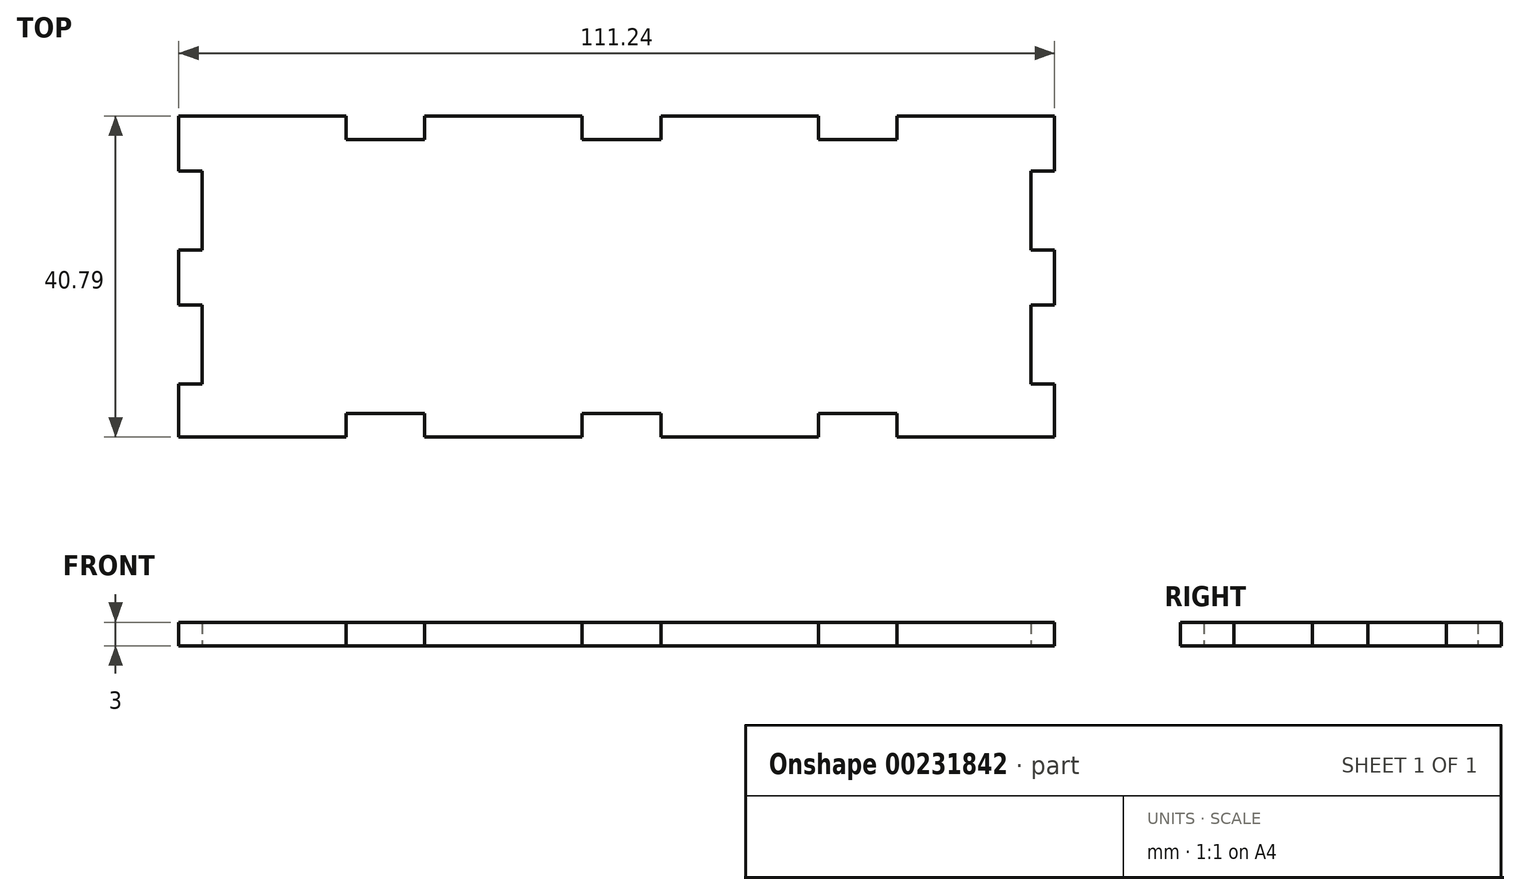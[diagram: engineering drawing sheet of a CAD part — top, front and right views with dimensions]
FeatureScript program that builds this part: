
annotation { "Feature Type Name" : "Feature", "Feature Type Description" : "" }
export const myFeature = defineFeature(function(context is Context, id is Id, definition is map)
    precondition{}
    {
        {
            var Q0;
            Q0=qCreatedBy(makeId("Top.planeOp"),FACE);
            var sketch = newSketch(context, id + "F0", { "sketchPlane" : qUnion([Q0])});
            skLineSegment(sketch, "E0", {"start": v(0, 0) * mm, "end": v(0, 7) * mm});
            skLineSegment(sketch, "E1", {"start": v(0, 7) * mm, "end": v(-3, 7) * mm});
            skLineSegment(sketch, "E2", {"start": v(-3, 7) * mm, "end": v(-3, 17) * mm});
            skLineSegment(sketch, "E3", {"start": v(0, 17) * mm, "end": v(-3, 17) * mm});
            skLineSegment(sketch, "E4", {"start": v(0, 17) * mm, "end": v(0, 24) * mm});
            skLineSegment(sketch, "E5", {"start": v(0, 24) * mm, "end": v(-3, 24) * mm});
            skLineSegment(sketch, "E6", {"start": v(-3, 24) * mm, "end": v(-3, 34) * mm});
            skLineSegment(sketch, "E7", {"start": v(-3, 34) * mm, "end": v(0, 34) * mm});
            skLineSegment(sketch, "E8", {"start": v(0, 34) * mm, "end": v(0, 41) * mm});
            skLineSegment(sketch, "E9", {"start": v(0, 41) * mm, "end": v(-20, 41) * mm});
            skLineSegment(sketch, "E10", {"start": v(-20, 41) * mm, "end": v(-20, 38) * mm});
            skLineSegment(sketch, "E11", {"start": v(-20, 38) * mm, "end": v(-30, 38) * mm});
            skLineSegment(sketch, "E12", {"start": v(-30, 41) * mm, "end": v(-30, 38) * mm});
            skLineSegment(sketch, "E13", {"start": v(-30, 41) * mm, "end": v(-50, 41) * mm});
            skLineSegment(sketch, "E14", {"start": v(-50, 38) * mm, "end": v(-50, 41) * mm});
            skLineSegment(sketch, "E15", {"start": v(-50, 38) * mm, "end": v(-60, 38) * mm});
            skLineSegment(sketch, "E16", {"start": v(-60, 38) * mm, "end": v(-60, 41) * mm});
            skLineSegment(sketch, "E17", {"start": v(-60, 41) * mm, "end": v(-80, 41) * mm});
            skLineSegment(sketch, "E18", {"start": v(-80, 38) * mm, "end": v(-80, 41) * mm});
            skLineSegment(sketch, "E19", {"start": v(-80, 38) * mm, "end": v(-90, 38) * mm});
            skLineSegment(sketch, "E20", {"start": v(-90, 41) * mm, "end": v(-90, 38) * mm});
            skLineSegment(sketch, "E21", {"start": v(-90, 41) * mm, "end": v(-110, 41) * mm});
            skLineSegment(sketch, "E22.MirrorCS", {"start": v(-50, 3.2) * mm, "end": v(-50, 0.2) * mm});
            skLineSegment(sketch, "E23.MirrorCS", {"start": v(-60, 3.2) * mm, "end": v(-60, 0.2) * mm});
            skLineSegment(sketch, "E24.MirrorCS", {"start": v(-80, 3.2) * mm, "end": v(-80, 0.2) * mm});
            skLineSegment(sketch, "E25.MirrorCS", {"start": v(-90, 0.2) * mm, "end": v(-90, 3.2) * mm});
            skLineSegment(sketch, "E26.MirrorCS", {"start": v(-20, 0.2) * mm, "end": v(-20, 3.2) * mm});
            skLineSegment(sketch, "E27.MirrorCS", {"start": v(-30, 0.2) * mm, "end": v(-30, 3.2) * mm});
            skLineSegment(sketch, "E28.MirrorCS", {"start": v(-90, 0.2) * mm, "end": v(-110, 0.2) * mm});
            skLineSegment(sketch, "E29.MirrorCS", {"start": v(-50, 3.2) * mm, "end": v(-60, 3.2) * mm});
            skLineSegment(sketch, "E30.MirrorCS", {"start": v(-30, 0.2) * mm, "end": v(-50, 0.2) * mm});
            skLineSegment(sketch, "E31.MirrorCS", {"start": v(-60, 0.2) * mm, "end": v(-80, 0.2) * mm});
            skLineSegment(sketch, "E32.MirrorCS", {"start": v(0, 0.2) * mm, "end": v(-20, 0.2) * mm});
            skLineSegment(sketch, "E33.MirrorCS", {"start": v(0, 7.2) * mm, "end": v(0, 0.2) * mm});
            skLineSegment(sketch, "E34.MirrorCS", {"start": v(-80, 3.2) * mm, "end": v(-90, 3.2) * mm});
            skLineSegment(sketch, "E35.MirrorCS", {"start": v(-20, 3.2) * mm, "end": v(-30, 3.2) * mm});
            skLineSegment(sketch, "E36.MirrorCS", {"start": v(-111.24, 7) * mm, "end": v(-108.24, 7) * mm});
            skLineSegment(sketch, "E37.MirrorCS", {"start": v(-108.24, 34) * mm, "end": v(-111.24, 34) * mm});
            skLineSegment(sketch, "E38.MirrorCS", {"start": v(-111.24, 17) * mm, "end": v(-108.24, 17) * mm});
            skLineSegment(sketch, "E39.MirrorCS", {"start": v(-111.24, 24) * mm, "end": v(-108.24, 24) * mm});
            skLineSegment(sketch, "E40.MirrorCS", {"start": v(-111.24, 0) * mm, "end": v(-111.24, 7) * mm});
            skLineSegment(sketch, "E41.MirrorCS", {"start": v(-111.24, 7.2) * mm, "end": v(-111.24, 0.2) * mm});
            skLineSegment(sketch, "E42.MirrorCS", {"start": v(-111.24, 34) * mm, "end": v(-111.24, 41) * mm});
            skLineSegment(sketch, "E43.MirrorCS", {"start": v(-108.24, 24) * mm, "end": v(-108.24, 34) * mm});
            skLineSegment(sketch, "E44.MirrorCS", {"start": v(-111.24, 17) * mm, "end": v(-111.24, 24) * mm});
            skLineSegment(sketch, "E45.MirrorCS", {"start": v(-108.24, 7) * mm, "end": v(-108.24, 17) * mm});
            skLineSegment(sketch, "E46", {"start": v(-111.24, 0.2) * mm, "end": v(-110, 0.2) * mm});
            skLineSegment(sketch, "E47", {"start": v(-111.24, 41) * mm, "end": v(-110, 41) * mm});
            skSolve(sketch);
        }
        {
            var Q0;
            {var subQ1=sQuery(id+"F0.wireOp",EDGE,"E1");Q0=makeQuery(id+"F0.imprint","IMPRINT",FACE,{"disambiguationData":[TD([[makeQuery(id+"F0.imprint","IMPRINT",EDGE,{"derivedFrom":subQ1}),1.0]])]});}
            extrude(context, id + "F1", {"entities" : qUnion([Q0]), "depth" : 3 * mm});
        }
    });
